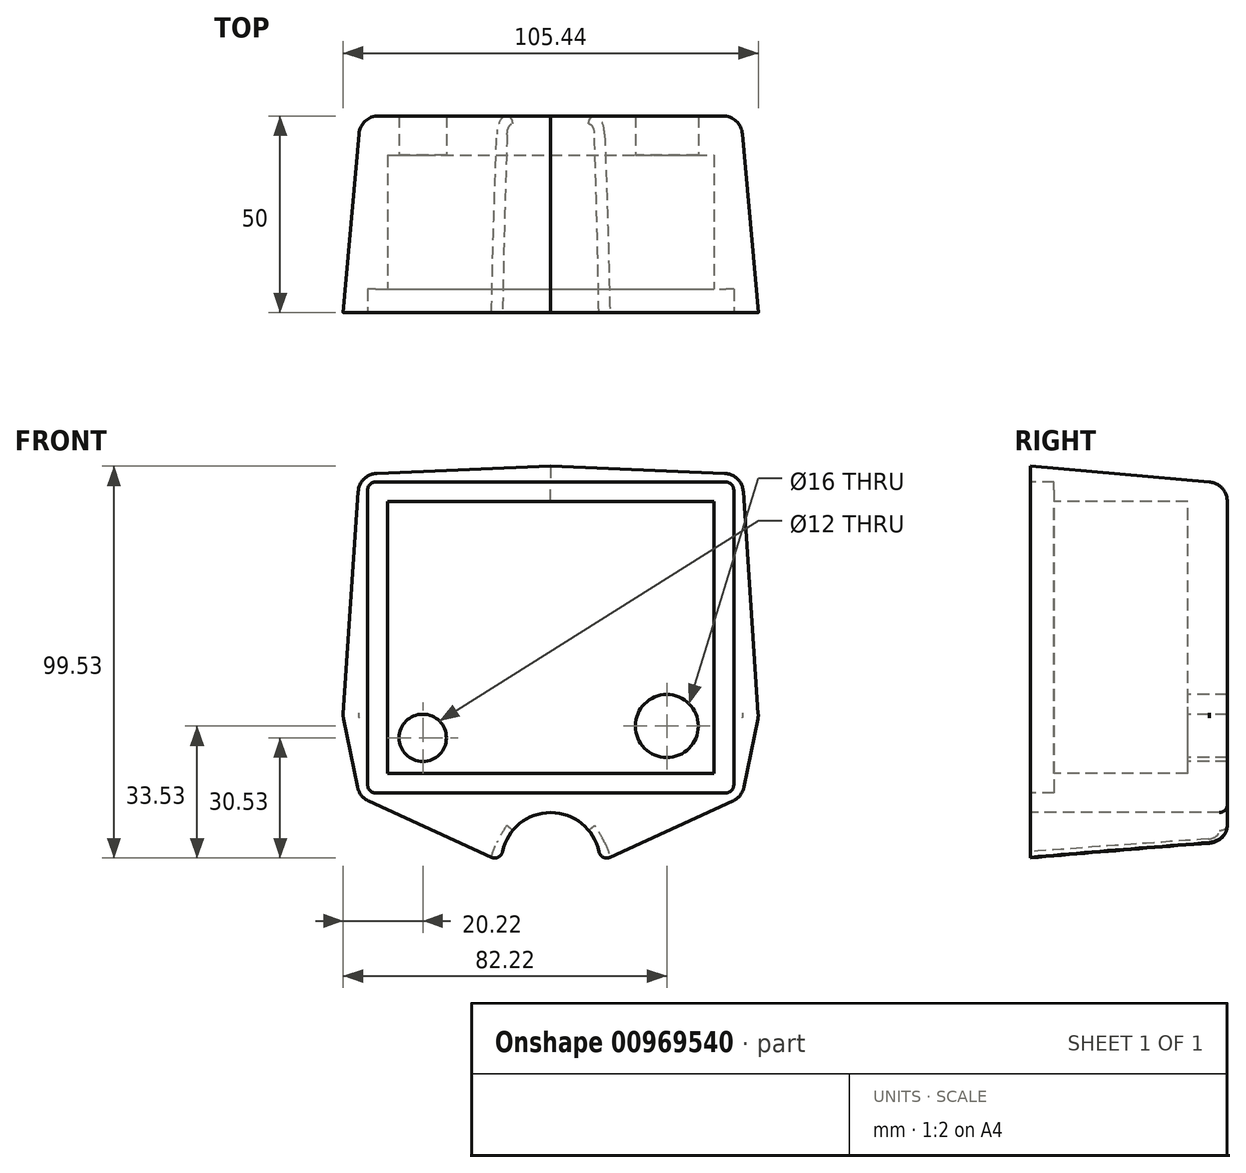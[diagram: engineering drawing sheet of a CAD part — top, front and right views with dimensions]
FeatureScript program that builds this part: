
annotation { "Feature Type Name" : "Feature", "Feature Type Description" : "" }
export const myFeature = defineFeature(function(context is Context, id is Id, definition is map)
    precondition{}
    {
        {
            var Q0;
            Q0=qCreatedBy(makeId("Front.planeOp"),FACE);
            var sketch = newSketch(context, id + "F0", { "sketchPlane" : qUnion([Q0])});
            skLineSegment(sketch, "E0.bottom", {"start": v(-44.5, 39.5) * mm, "end": v(44.5, 39.5) * mm});
            skLineSegment(sketch, "E0.top", {"start": v(-44.5, -39.5) * mm, "end": v(44.5, -39.5) * mm});
            skLineSegment(sketch, "E0.left", {"start": v(-46.5, 37.5) * mm, "end": v(-46.5, -37.5) * mm});
            skLineSegment(sketch, "E0.right", {"start": v(46.5, 37.5) * mm, "end": v(46.5, -37.5) * mm});
            skPoint(sketch, "E1.middle", {"position": v(0, 0) * mm});
            skPoint(sketch, "E1.middle.positionSnap0", {"position": v(-46.5, 0) * mm});
            skPoint(sketch, "E1.middle.positionSnap1", {"position": v(0, 39.5) * mm});
            skPoint(sketch, "E1.centerSnap0", {"position": v(-46.5, 0) * mm});
            skPoint(sketch, "E1.centerSnap1", {"position": v(0, 39.5) * mm});
            skLineSegment(sketch, "E2", {"start": v(0, 55.5) * mm, "end": v(0, -44.5) * mm, "construction": true});
            skLineSegment(sketch, "E3", {"start": v(-48.86, 0.37) * mm, "end": v(-48.86, 0.37) * mm});
            skArc(sketch, "E4", {"start": v(12.5, -57) * mm, "mid": v(0, -44.5) * mm, "end": v(-12.5, -57) * mm});
            skLineSegment(sketch, "E5", {"start": v(-12.5, -57) * mm, "end": v(12.5, -57) * mm});
            skLineSegment(sketch, "E6.bottom", {"start": v(-41.5, -34.5) * mm, "end": v(41.5, -34.5) * mm});
            skLineSegment(sketch, "E6.top", {"start": v(-41.5, 34.5) * mm, "end": v(41.5, 34.5) * mm});
            skLineSegment(sketch, "E6.left", {"start": v(-41.5, -34.5) * mm, "end": v(-41.5, 34.5) * mm});
            skLineSegment(sketch, "E6.right", {"start": v(41.5, -34.5) * mm, "end": v(41.5, 34.5) * mm});
            skPoint(sketch, "E7.visualSharp", {"position": v(46.5, 39.5) * mm});
            skArc(sketch, "E7.filletArc", {"start": v(46.5, 37.5) * mm, "mid": v(45.91, 38.91) * mm, "end": v(44.5, 39.5) * mm});
            skPoint(sketch, "E8.visualSharp", {"position": v(-46.5, 39.5) * mm});
            skArc(sketch, "E8.filletArc", {"start": v(-44.5, 39.5) * mm, "mid": v(-45.91, 38.91) * mm, "end": v(-46.5, 37.5) * mm});
            skPoint(sketch, "E9.visualSharp", {"position": v(46.5, -39.5) * mm});
            skArc(sketch, "E9.filletArc", {"start": v(44.5, -39.5) * mm, "mid": v(45.91, -38.91) * mm, "end": v(46.5, -37.5) * mm});
            skPoint(sketch, "E10.visualSharp", {"position": v(-46.5, -39.5) * mm});
            skArc(sketch, "E10.filletArc", {"start": v(-46.5, -37.5) * mm, "mid": v(-45.91, -38.91) * mm, "end": v(-44.5, -39.5) * mm});
            skLineSegment(sketch, "E11", {"start": v(0, 0) * mm, "end": v(-76.64, -63.9) * mm, "construction": true});
            skLineSegment(sketch, "E12", {"start": v(0, 0) * mm, "end": v(-55.32, 47.26) * mm, "construction": true});
            skLineSegment(sketch, "E13", {"start": v(-12.5, -57) * mm, "end": v(-48.58, -40.5) * mm});
            skLineSegment(sketch, "E14", {"start": v(-48.58, -40.5) * mm, "end": v(-52.76, -20.1) * mm});
            skLineSegment(sketch, "E15", {"start": v(-52.76, -20.1) * mm, "end": v(-48.6, 41.53) * mm});
            skLineSegment(sketch, "E16", {"start": v(-48.6, 41.53) * mm, "end": v(0, 43.5) * mm});
            skLineSegment(sketch, "E17.MirrorCS", {"start": v(48.6, 41.53) * mm, "end": v(0, 43.5) * mm});
            skLineSegment(sketch, "E18.MirrorCS", {"start": v(52.76, -20.1) * mm, "end": v(48.6, 41.53) * mm});
            skLineSegment(sketch, "E19.MirrorCS", {"start": v(48.58, -40.5) * mm, "end": v(52.76, -20.1) * mm});
            skLineSegment(sketch, "E20.MirrorCS", {"start": v(12.5, -57) * mm, "end": v(48.58, -40.5) * mm});
            skSolve(sketch);
        }
        {
            var Q0;
            Q0=makeQuery(id+"F0.imprint","IMPRINT",FACE,{"disambiguationData":[TD([[makeQuery(id+"F0.imprint","IMPRINT",EDGE,{"derivedFrom":sQuery(id+"F0.wireOp",EDGE,"E0.bottom")}),1.0]])]});
            var Q1;
            Q1=makeQuery(id+"F0.imprint","IMPRINT",FACE,{"disambiguationData":[TD([[makeQuery(id+"F0.imprint","IMPRINT",EDGE,{"derivedFrom":sQuery(id+"F0.wireOp",EDGE,"E0.bottom")}),-1.0]])]});
            var Q2;
            Q2=makeQuery(id+"F0.imprint","IMPRINT",FACE,{"disambiguationData":[TD([[makeQuery(id+"F0.imprint","IMPRINT",EDGE,{"derivedFrom":sQuery(id+"F0.wireOp",EDGE,"E6.bottom")}),1.0]])]});
            var Q3;
            Q3=makeQuery(id+"F0.imprint","IMPRINT",FACE,{"disambiguationData":[TD([[makeQuery(id+"F0.imprint","IMPRINT",EDGE,{"derivedFrom":sQuery(id+"F0.wireOp",EDGE,"E4")}),1.0]])]});
            extrude(context, id + "F1", {"entities" : qUnion([Q0, Q1, Q2, Q3]), "oppositeDirection" : true, "depth" : 50 * mm, "offsetDistance" : 25 * mm, "hasDraft" : true, "draftAngle" : 5 * degree, "draftPullDirection" : true});
        }
        {
            var Q0;
            Q0=makeQuery(id+"F0.imprint","IMPRINT",FACE,{"disambiguationData":[TD([[makeQuery(id+"F0.imprint","IMPRINT",EDGE,{"derivedFrom":sQuery(id+"F0.wireOp",EDGE,"E4")}),1.0]])]});
            extrude(context, id + "F2", {"entities" : qUnion([Q0]), "operationType" : NewBodyOperationType.REMOVE, "oppositeDirection" : true, "depth" : 50 * mm, "offsetDistance" : 25 * mm});
        }
        {
            var Q0;
            Q0=makeQuery(id+"F0.imprint","IMPRINT",FACE,{"disambiguationData":[TD([[makeQuery(id+"F0.imprint","IMPRINT",EDGE,{"derivedFrom":sQuery(id+"F0.wireOp",EDGE,"E0.bottom")}),-1.0]])]});
            var Q1;
            Q1=makeQuery(id+"F0.imprint","IMPRINT",FACE,{"disambiguationData":[TD([[makeQuery(id+"F0.imprint","IMPRINT",EDGE,{"derivedFrom":sQuery(id+"F0.wireOp",EDGE,"E6.bottom")}),1.0]])]});
            extrude(context, id + "F3", {"entities" : qUnion([Q0, Q1]), "operationType" : NewBodyOperationType.REMOVE, "oppositeDirection" : true, "depth" : 6 * mm, "offsetDistance" : 25 * mm});
        }
        {
            var Q0;
            Q0=makeQuery(id+"F0.imprint","IMPRINT",FACE,{"disambiguationData":[TD([[makeQuery(id+"F0.imprint","IMPRINT",EDGE,{"derivedFrom":sQuery(id+"F0.wireOp",EDGE,"E6.bottom")}),1.0]])]});
            extrude(context, id + "F4", {"entities" : qUnion([Q0]), "operationType" : NewBodyOperationType.REMOVE, "oppositeDirection" : true, "depth" : 40 * mm, "offsetDistance" : 25 * mm});
        }
        {
            var Q0;
            Q0=makeQuery(id+"F4.boolean.opBoolean","COPY",FACE,{"derivedFrom":makeQuery(id+"F4.opExtrude","CAP_FACE",FACE,{"disambiguationData":[OSD([sQuery(id+"F0.wireOp",EDGE,"E6.bottom"),sQuery(id+"F0.wireOp",EDGE,"E6.top"),sQuery(id+"F0.wireOp",EDGE,"E6.left"),sQuery(id+"F0.wireOp",EDGE,"E6.right")])],"isStart":false})});
            var sketch = newSketch(context, id + "F5", { "sketchPlane" : qUnion([Q0])});
            skCircle(sketch, "E21", {"center": v(-32.5, -25.5) * mm, "radius": 8 * mm});
            skCircle(sketch, "E22", {"center": v(-32.5, -25.5) * mm, "radius": 6 * mm});
            skCircle(sketch, "E23", {"center": v(29.5, -22.5) * mm, "radius": 11 * mm});
            skCircle(sketch, "E24", {"center": v(29.5, -22.5) * mm, "radius": 8 * mm});
            skSolve(sketch);
        }
        {
            var Q0;
            Q0=makeQuery(id+"F5.imprint","IMPRINT",FACE,{"disambiguationData":[TD([[makeQuery(id+"F5.imprint","IMPRINT",EDGE,{"derivedFrom":sQuery(id+"F5.wireOp",EDGE,"E22")}),1.0]])]});
            var Q1;
            Q1=makeQuery(id+"F5.imprint","IMPRINT",FACE,{"disambiguationData":[TD([[makeQuery(id+"F5.imprint","IMPRINT",EDGE,{"derivedFrom":sQuery(id+"F5.wireOp",EDGE,"E24")}),1.0]])]});
            extrude(context, id + "F6", {"entities" : qUnion([Q0, Q1]), "operationType" : NewBodyOperationType.REMOVE, "endBound" : BoundingType.UP_TO_NEXT, "oppositeDirection" : true, "depth" : 25 * mm, "offsetDistance" : 25 * mm});
        }
        {
            var Q0;
            Q0=makeQuery(id+"F1.opExtrude","CAP_EDGE",EDGE,{"disambiguationData":[OSD([sQuery(id+"F0.wireOp",EDGE,"E18.MirrorCS")])],"isStart":false});
            var Q1;
            Q1=makeQuery(id+"F1.opExtrude","CAP_EDGE",EDGE,{"disambiguationData":[OSD([sQuery(id+"F0.wireOp",EDGE,"E20.MirrorCS")])],"isStart":false});
            var Q2;
            Q2=makeQuery(id+"F1.opExtrude","CAP_EDGE",EDGE,{"disambiguationData":[OSD([sQuery(id+"F0.wireOp",EDGE,"E13")])],"isStart":false});
            var Q3;
            Q3=makeQuery(id+"F1.opExtrude","CAP_EDGE",EDGE,{"disambiguationData":[OSD([sQuery(id+"F0.wireOp",EDGE,"E15")])],"isStart":false});
            var Q4;
            Q4=makeQuery(id+"F1.opExtrude","CAP_EDGE",EDGE,{"disambiguationData":[OSD([sQuery(id+"F0.wireOp",EDGE,"E17.MirrorCS")])],"isStart":false});
            var Q5;
            Q5=makeQuery(id+"F1.opExtrude","CAP_EDGE",EDGE,{"disambiguationData":[OSD([sQuery(id+"F0.wireOp",EDGE,"E14")])],"isStart":false});
            var Q6;
            Q6=makeQuery(id+"F1.opExtrude","CAP_EDGE",EDGE,{"disambiguationData":[OSD([sQuery(id+"F0.wireOp",EDGE,"E19.MirrorCS")])],"isStart":false});
            var Q7;
            Q7=makeQuery(id+"F1.opExtrude","SWEPT_EDGE",EDGE,{"disambiguationData":[OSD([sQuery(id+"F0.wireOp",EDGE,"E13"),sQuery(id+"F0.wireOp",EDGE,"E14")])]});
            var Q8;
            Q8=makeQuery(id+"F1.opExtrude","SWEPT_EDGE",EDGE,{"disambiguationData":[OSD([sQuery(id+"F0.wireOp",EDGE,"E19.MirrorCS"),sQuery(id+"F0.wireOp",EDGE,"E20.MirrorCS")])]});
            var Q9;
            Q9=makeQuery(id+"F1.opExtrude","SWEPT_EDGE",EDGE,{"disambiguationData":[OSD([sQuery(id+"F0.wireOp",EDGE,"E17.MirrorCS"),sQuery(id+"F0.wireOp",EDGE,"E18.MirrorCS")])]});
            var Q10;
            Q10=makeQuery(id+"F1.opExtrude","SWEPT_EDGE",EDGE,{"disambiguationData":[OSD([sQuery(id+"F0.wireOp",EDGE,"E15"),sQuery(id+"F0.wireOp",EDGE,"E16")])]});
            var Q11;
            Q11=makeQuery(id+"F1.opExtrude","CAP_EDGE",EDGE,{"disambiguationData":[OSD([sQuery(id+"F0.wireOp",EDGE,"E16")])],"isStart":false});
            var Q12;
            Q12=makeQuery(id+"F1.opExtrude","SWEPT_EDGE",EDGE,{"disambiguationData":[OSD([sQuery(id+"F0.wireOp",EDGE,"E14"),sQuery(id+"F0.wireOp",EDGE,"E15")])]});
            var Q13;
            Q13=makeQuery(id+"F1.opExtrude","SWEPT_EDGE",EDGE,{"disambiguationData":[OSD([sQuery(id+"F0.wireOp",EDGE,"E18.MirrorCS"),sQuery(id+"F0.wireOp",EDGE,"E19.MirrorCS")])]});
            fillet(context, id + "F7", {"entities" : qUnion([Q0, Q1, Q2, Q3, Q4, Q5, Q6, Q7, Q8, Q9, Q10, Q11, Q12, Q13]), "radius" : 5 * mm, "tangentPropagation" : true, "allowEdgeOverflow" : false});
        }
        {
            var Q0;
            Q0=makeQuery(id+"F2.boolean.opBoolean","INTERSECT",EDGE,{"derivedFrom":[makeQuery(id+"F1.opExtrude","SWEPT_FACE",FACE,{"disambiguationData":[OSD([sQuery(id+"F0.wireOp",EDGE,"E13")])]}),makeQuery(id+"F2.opExtrude","SWEPT_FACE",FACE,{"disambiguationData":[OSD([sQuery(id+"F0.wireOp",EDGE,"E4")])]})]});
            fillet(context, id + "F8", {"entities" : qUnion([Q0]), "radius" : 2 * mm, "tangentPropagation" : true, "allowEdgeOverflow" : false});
        }
    });
